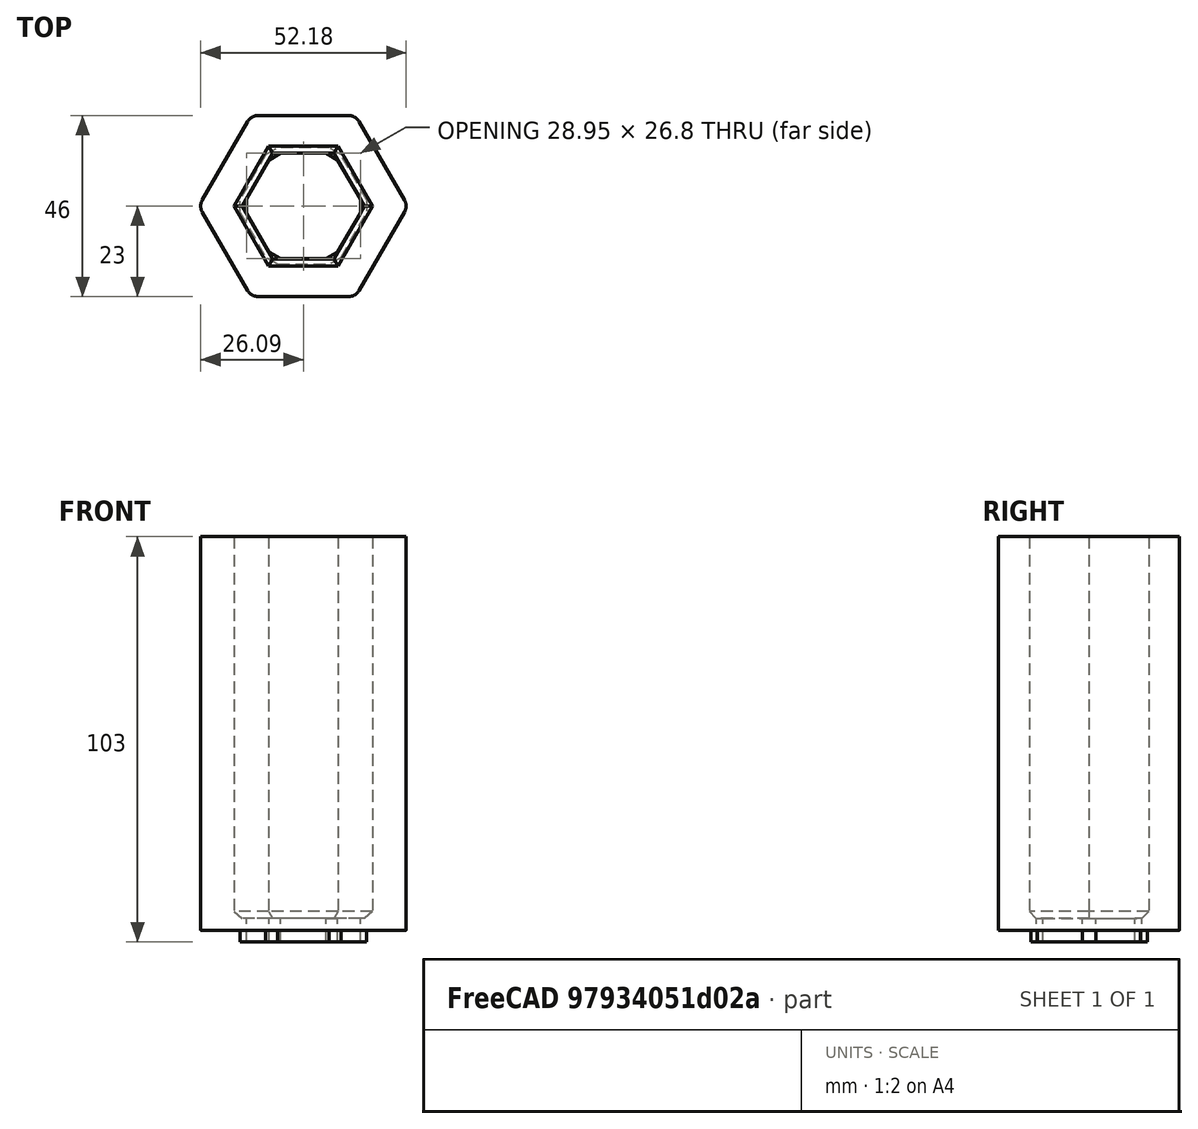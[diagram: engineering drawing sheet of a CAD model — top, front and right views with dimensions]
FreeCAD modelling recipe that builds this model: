
FCSTD DOCUMENT  (FreeCAD 0.18R16131 (Git))
Label: Marble_Run_Spacer
License: All rights reserved
LicenseURL: http://en.wikipedia.org/wiki/All_rights_reserved
objects: Sketcher::SketchObject×4, PartDesign::Chamfer×3, PartDesign::Pad×2, PartDesign::Pocket×2, Spreadsheet::Sheet×1, PartDesign::Fillet×1, PartDesign::Body×1, Mesh::Feature×1
note: 17 computed .brp shape members not serialized (recipe doc carries the construction recipe); baked Part::Feature solids carry a one-line shape summary decoded from their .brp

FEATURE [Sketcher::SketchObject] Sketch
  MapMode = 5
  Support = -> [XY_Plane]
  expr: Constraints[8] = Measures.B2
  expr: Constraints[9] = Measures.B2
  expr: Constraints[15] = Measures.B2 * 2 / sqrt(3) / 2
  expr: Constraints[11] = Measures.B2 / 2
  expr: Constraints[10] = Measures.B2 / 2
  sketch-geometry (11):
    g0: LineSegment [constr] StartX=-23 StartY=23 StartZ=0 EndX=23 EndY=23 EndZ=0
    g1: LineSegment [constr] StartX=23 StartY=23 StartZ=0 EndX=23 EndY=-23 EndZ=0
    g2: LineSegment [constr] StartX=23 StartY=-23 StartZ=0 EndX=-23 EndY=-23 EndZ=0
    g3: LineSegment [constr] StartX=-23 StartY=-23 StartZ=0 EndX=-23 EndY=23 EndZ=0
    g4: LineSegment StartX=13.2791 StartY=-23 StartZ=0 EndX=-13.2791 EndY=-23 EndZ=0
    g5: Circle [constr] CenterX=0 CenterY=0 CenterZ=0 NormalX=0 NormalY=0 NormalZ=1 AngleXU=0 Radius=26.5581
    g6: LineSegment StartX=-13.2791 StartY=-23 StartZ=0 EndX=-26.5581 EndY=0 EndZ=0
    g7: LineSegment StartX=-26.5581 StartY=0 StartZ=0 EndX=-13.2791 EndY=23 EndZ=0
    g8: LineSegment StartX=-13.2791 StartY=23 StartZ=0 EndX=13.2791 EndY=23 EndZ=0
    g9: LineSegment StartX=13.2791 StartY=23 StartZ=0 EndX=26.5581 EndY=0 EndZ=0
    g10: LineSegment StartX=26.5581 StartY=0 StartZ=0 EndX=13.2791 EndY=-23 EndZ=0
  constraints (32):
    c: Coincident(g0,g1)
    c: Coincident(g1,g2)
    c: Coincident(g2,g3)
    c: Coincident(g3,g0)
    c: Horizontal(g0)
    c: Horizontal(g2)
    c: Vertical(g1)
    c: Vertical(g3)
    c: DistanceX(g2,g2) = 46
    c: DistanceY(g3,g3) = 46
    c: Distance(g-1,g3) = 23
    c: Distance(g-1,g0) = 23
    c: PointOnObject(g4,g2)
    c: PointOnObject(g4,g2)
    c: Coincident(g5,g-1)
    c: Radius(g5) = 26.5581
    c: PointOnObject(g4,g5)
    c: PointOnObject(g4,g5)
    c: Coincident(g6,g4)
    c: PointOnObject(g6,g5)
    c: PointOnObject(g6,g-1)
    c: Coincident(g7,g6)
    c: PointOnObject(g7,g0)
    c: PointOnObject(g7,g5)
    c: Coincident(g8,g7)
    c: PointOnObject(g8,g5)
    c: Horizontal(g8)
    c: Coincident(g9,g8)
    c: PointOnObject(g9,g5)
    c: PointOnObject(g9,g-1)
    c: Coincident(g10,g9)
    c: Coincident(g10,g4)
FEATURE [Spreadsheet::Sheet] Spreadsheet  label="Measures"
  cells = A1=Height (Units); B1=Wrench Size Outer; C1=Wrench Size Upper; D1=Wrench Size Lower; E1=Wrench Size Inner; F1=Camfer Lower; G1=Camfer Inner; A2=10; B2=46; C2=30.4; D2=29.6; E2==D2 - 2.8; F2=2; G2==(C2 - E2) / 2 - 0.05
FEATURE [PartDesign::Pad] Pad
  Length = 100
  Length2 = 100
  Profile = -> Sketch
  Type = 0
  expr: Length = Measures.A2 * 10
FEATURE [Sketcher::SketchObject] Sketch001
  MapMode = 5
  Placement = pos=(0,0,100) rot=(0,0,1;0rad)
  Support = -> [Pad]
  expr: Constraints[13] = Measures.C2 * 2 / sqrt(3) / 2
  expr: Constraints[11] = Measures.C2 / 2
  expr: Constraints[10] = Measures.C2
  expr: Constraints[12] = Measures.C2 / 2
  expr: Constraints[9] = Measures.C2
  sketch-geometry (11):
    g0: LineSegment [constr] StartX=-15.2 StartY=15.2 StartZ=0 EndX=15.2 EndY=15.2 EndZ=0
    g1: LineSegment [constr] StartX=15.2 StartY=15.2 StartZ=0 EndX=15.2 EndY=-15.2 EndZ=0
    g2: LineSegment [constr] StartX=15.2 StartY=-15.2 StartZ=0 EndX=-15.2 EndY=-15.2 EndZ=0
    g3: LineSegment [constr] StartX=-15.2 StartY=-15.2 StartZ=0 EndX=-15.2 EndY=15.2 EndZ=0
    g4: Circle [constr] CenterX=0 CenterY=0 CenterZ=0 NormalX=0 NormalY=0 NormalZ=1 AngleXU=0 Radius=17.5514
    g5: LineSegment StartX=8.77572 StartY=-15.2 StartZ=0 EndX=-8.77572 EndY=-15.2 EndZ=0
    g6: LineSegment StartX=-8.77572 StartY=-15.2 StartZ=0 EndX=-17.5514 EndY=-1.8e-15 EndZ=0
    g7: LineSegment StartX=-17.5514 StartY=-1.8e-15 StartZ=0 EndX=-8.77572 EndY=15.2 EndZ=0
    g8: LineSegment StartX=-8.77572 StartY=15.2 StartZ=0 EndX=8.77572 EndY=15.2 EndZ=0
    g9: LineSegment StartX=8.77572 StartY=15.2 StartZ=0 EndX=17.5514 EndY=0 EndZ=0
    g10: LineSegment StartX=17.5514 StartY=0 StartZ=0 EndX=8.77572 EndY=-15.2 EndZ=0
  constraints (32):
    c: Coincident(g0,g1)
    c: Coincident(g1,g2)
    c: Coincident(g2,g3)
    c: Coincident(g3,g0)
    c: Horizontal(g0)
    c: Horizontal(g2)
    c: Vertical(g1)
    c: Vertical(g3)
    c: Coincident(g4,g-1)
    c: DistanceX(g2,g2) = 30.4
    c: DistanceY(g3,g3) = 30.4
    c: Distance(g4,g3) = 15.2
    c: Distance(g4,g2) = 15.2
    c: Radius(g4) = 17.5514
    c: PointOnObject(g5,g2)
    c: PointOnObject(g5,g2)
    c: PointOnObject(g5,g4)
    c: PointOnObject(g5,g4)
    c: Coincident(g6,g5)
    c: PointOnObject(g6,g-1)
    c: PointOnObject(g6,g4)
    c: Coincident(g7,g6)
    c: PointOnObject(g7,g0)
    c: PointOnObject(g7,g4)
    c: Coincident(g8,g7)
    c: PointOnObject(g8,g0)
    c: PointOnObject(g8,g4)
    c: Coincident(g9,g8)
    c: PointOnObject(g9,g4)
    c: PointOnObject(g9,g-1)
    c: Coincident(g10,g9)
    c: Coincident(g10,g5)
FEATURE [PartDesign::Pocket] Pocket
  BaseFeature = -> Pad
  Length = 97
  Length2 = 100
  Profile = -> Sketch001
  Type = 0
  expr: Length = Measures.A2 * 10 - 3
FEATURE [Sketcher::SketchObject] Sketch002
  MapMode = 5
  Placement = pos=(0,0,0) rot=(1,0,0;3.14159rad)
  Support = -> [Pocket]
  expr: Constraints[8] = Measures.D2
  expr: Constraints[13] = Measures.D2 * 2 / sqrt(3) / 2
  expr: Constraints[11] = Measures.D2 / 2
  expr: Constraints[10] = Measures.D2 / 2
  expr: Constraints[9] = Measures.D2
  sketch-geometry (11):
    g0: LineSegment [constr] StartX=-14.8 StartY=14.8 StartZ=0 EndX=14.8 EndY=14.8 EndZ=0
    g1: LineSegment [constr] StartX=14.8 StartY=14.8 StartZ=0 EndX=14.8 EndY=-14.8 EndZ=0
    g2: LineSegment [constr] StartX=14.8 StartY=-14.8 StartZ=0 EndX=-14.8 EndY=-14.8 EndZ=0
    g3: LineSegment [constr] StartX=-14.8 StartY=-14.8 StartZ=0 EndX=-14.8 EndY=14.8 EndZ=0
    g4: Circle [constr] CenterX=0 CenterY=0 CenterZ=0 NormalX=0 NormalY=0 NormalZ=1 AngleXU=0 Radius=17.0896
    g5: LineSegment StartX=8.54478 StartY=-14.8 StartZ=0 EndX=-8.54478 EndY=-14.8 EndZ=0
    g6: LineSegment StartX=-8.54478 StartY=-14.8 StartZ=0 EndX=-17.0896 EndY=0 EndZ=0
    g7: LineSegment StartX=-17.0896 StartY=0 StartZ=0 EndX=-8.54478 EndY=14.8 EndZ=0
    g8: LineSegment StartX=-8.54478 StartY=14.8 StartZ=0 EndX=8.54478 EndY=14.8 EndZ=0
    g9: LineSegment StartX=8.54478 StartY=14.8 StartZ=0 EndX=17.0896 EndY=0 EndZ=0
    g10: LineSegment StartX=17.0896 StartY=0 StartZ=0 EndX=8.54478 EndY=-14.8 EndZ=0
  constraints (32):
    c: Coincident(g0,g1)
    c: Coincident(g1,g2)
    c: Coincident(g2,g3)
    c: Coincident(g3,g0)
    c: Horizontal(g0)
    c: Horizontal(g2)
    c: Vertical(g1)
    c: Vertical(g3)
    c: DistanceX(g2,g2) = 29.6
    c: DistanceY(g3,g3) = 29.6
    c: Distance(g-1,g3) = 14.8
    c: Distance(g-1,g2) = 14.8
    c: Coincident(g4,g-1)
    c: Radius(g4) = 17.0896
    c: PointOnObject(g5,g2)
    c: PointOnObject(g5,g2)
    c: PointOnObject(g5,g4)
    c: PointOnObject(g5,g4)
    c: Coincident(g6,g5)
    c: PointOnObject(g6,g4)
    c: PointOnObject(g6,g-1)
    c: Coincident(g7,g6)
    c: PointOnObject(g7,g4)
    c: PointOnObject(g7,g0)
    c: Coincident(g8,g7)
    c: PointOnObject(g8,g0)
    c: PointOnObject(g8,g4)
    c: Coincident(g9,g8)
    c: PointOnObject(g9,g4)
    c: PointOnObject(g9,g-1)
    c: Coincident(g10,g9)
    c: Coincident(g10,g5)
FEATURE [PartDesign::Pad] Pad001
  BaseFeature = -> Pocket
  Length = 3
  Length2 = 100
  Profile = -> Sketch002
  Type = 0
FEATURE [Sketcher::SketchObject] Sketch003
  MapMode = 5
  Placement = pos=(0,0,-3) rot=(1,0,0;3.14159rad)
  Support = -> [Pad001]
  expr: Constraints[13] = Measures.E2 * 2 / sqrt(3) / 2
  expr: Constraints[11] = Measures.E2 / 2
  expr: Constraints[10] = Measures.E2 / 2
  expr: Constraints[9] = Measures.E2
  expr: Constraints[8] = Measures.E2
  sketch-geometry (11):
    g0: LineSegment [constr] StartX=-13.4 StartY=13.4 StartZ=0 EndX=13.4 EndY=13.4 EndZ=0
    g1: LineSegment [constr] StartX=13.4 StartY=13.4 StartZ=0 EndX=13.4 EndY=-13.4 EndZ=0
    g2: LineSegment [constr] StartX=13.4 StartY=-13.4 StartZ=0 EndX=-13.4 EndY=-13.4 EndZ=0
    g3: LineSegment [constr] StartX=-13.4 StartY=-13.4 StartZ=0 EndX=-13.4 EndY=13.4 EndZ=0
    g4: Circle [constr] CenterX=0 CenterY=0 CenterZ=0 NormalX=0 NormalY=0 NormalZ=1 AngleXU=0 Radius=15.473
    g5: LineSegment StartX=7.73649 StartY=-13.4 StartZ=0 EndX=-7.73649 EndY=-13.4 EndZ=0
    g6: LineSegment StartX=-7.73649 StartY=-13.4 StartZ=0 EndX=-15.473 EndY=0 EndZ=0
    g7: LineSegment StartX=-15.473 StartY=0 StartZ=0 EndX=-7.73649 EndY=13.4 EndZ=0
    g8: LineSegment StartX=-7.73649 StartY=13.4 StartZ=0 EndX=7.73649 EndY=13.4 EndZ=0
    g9: LineSegment StartX=7.73649 StartY=13.4 StartZ=0 EndX=15.473 EndY=0 EndZ=0
    g10: LineSegment StartX=15.473 StartY=0 StartZ=0 EndX=7.73649 EndY=-13.4 EndZ=0
  constraints (32):
    c: Coincident(g0,g1)
    c: Coincident(g1,g2)
    c: Coincident(g2,g3)
    c: Coincident(g3,g0)
    c: Horizontal(g0)
    c: Horizontal(g2)
    c: Vertical(g1)
    c: Vertical(g3)
    c: DistanceX(g2,g2) = 26.8
    c: DistanceY(g3,g3) = 26.8
    c: Distance(g-1,g3) = 13.4
    c: Distance(g-1,g0) = 13.4
    c: Coincident(g4,g-1)
    c: Radius(g4) = 15.473
    c: PointOnObject(g5,g2)
    c: PointOnObject(g5,g2)
    c: PointOnObject(g5,g4)
    c: PointOnObject(g5,g4)
    c: Coincident(g6,g5)
    c: PointOnObject(g6,g4)
    c: PointOnObject(g6,g-1)
    c: Coincident(g7,g6)
    c: PointOnObject(g7,g4)
    c: PointOnObject(g7,g0)
    c: Coincident(g8,g7)
    c: PointOnObject(g8,g0)
    c: PointOnObject(g8,g4)
    c: Coincident(g9,g8)
    c: PointOnObject(g9,g4)
    c: PointOnObject(g9,g-1)
    c: Coincident(g10,g9)
    c: Coincident(g10,g5)
FEATURE [PartDesign::Pocket] Pocket001
  BaseFeature = -> Pad001
  Length = 5
  Length2 = 100
  Profile = -> Sketch003
  Type = 1
FEATURE [PartDesign::Chamfer] Chamfer
  Base = -> Pocket001 [Edge54,Edge53,Edge45,Edge51,Edge49,Edge47]
  BaseFeature = -> Pocket001
  Size = 1.75
  expr: Size = Measures.G2
FEATURE [PartDesign::Fillet] Fillet
  Base = -> Chamfer [Edge38,Edge41,Edge39,Edge43,Edge47,Edge45]
  BaseFeature = -> Chamfer
  Radius = 3
FEATURE [PartDesign::Chamfer] Chamfer001
  Base = -> Fillet [Edge82,Edge80,Edge78,Edge76,Edge73,Edge74]
  BaseFeature = -> Fillet
  Size = 2
  expr: Size = Measures.F2
FEATURE [PartDesign::Chamfer] Chamfer002
  Base = -> Chamfer001 [Edge87,Edge85,Edge94,Edge92,Edge90,Edge88]
  BaseFeature = -> Chamfer001
  Size = 2
  expr: Size = Measures.F2
FEATURE [PartDesign::Body] Body
  Group = -> [Sketch,Pad,Sketch001,Pocket,Sketch002,Pad001,Sketch003,Pocket001,Chamfer,Fillet,Chamfer001,Chamfer002]
  Origin = -> Origin
  Tip = -> Chamfer002
FEATURE [Mesh::Feature] Mesh  label="Marble_Run_Spacer"
